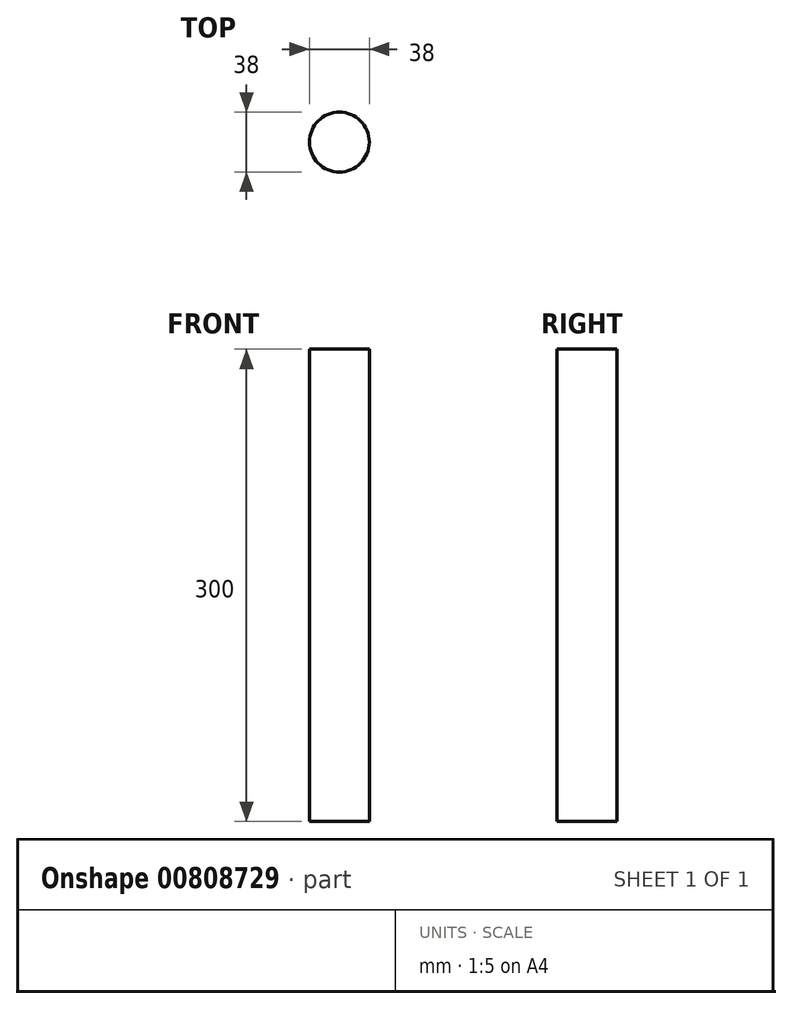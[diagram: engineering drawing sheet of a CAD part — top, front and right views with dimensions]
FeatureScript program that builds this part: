
annotation { "Feature Type Name" : "Feature", "Feature Type Description" : "" }
export const myFeature = defineFeature(function(context is Context, id is Id, definition is map)
    precondition{}
    {
        {
            var Q0;
            Q0=qCreatedBy(makeId("Top.planeOp"),FACE);
            var sketch = newSketch(context, id + "F0", { "sketchPlane" : qUnion([Q0])});
            skCircle(sketch, "E0", {"center": v(0, 0) * mm, "radius": 19 * mm});
            skSolve(sketch);
        }
        {
            var Q0;
            Q0=makeQuery(id+"F0.imprint","IMPRINT",FACE,{"disambiguationData":[TD([[makeQuery(id+"F0.imprint","IMPRINT",EDGE,{"derivedFrom":sQuery(id+"F0.wireOp",EDGE,"E0")}),1.0]])]});
            extrude(context, id + "F1", {"entities" : qUnion([Q0]), "depth" : 300 * mm, "offsetDistance" : 25 * mm});
        }
        {
            var Q0;
            Q0=makeQuery(id+"F1.opExtrude","CAP_FACE",FACE,{"disambiguationData":[OSD([sQuery(id+"F0.wireOp",EDGE,"E0")])],"isStart":false});
            var sketch = newSketch(context, id + "F2", { "sketchPlane" : qUnion([Q0])});
            skPoint(sketch, "E1.0", {"position": v(0, 0) * mm});
            skSolve(sketch);
        }
    });
